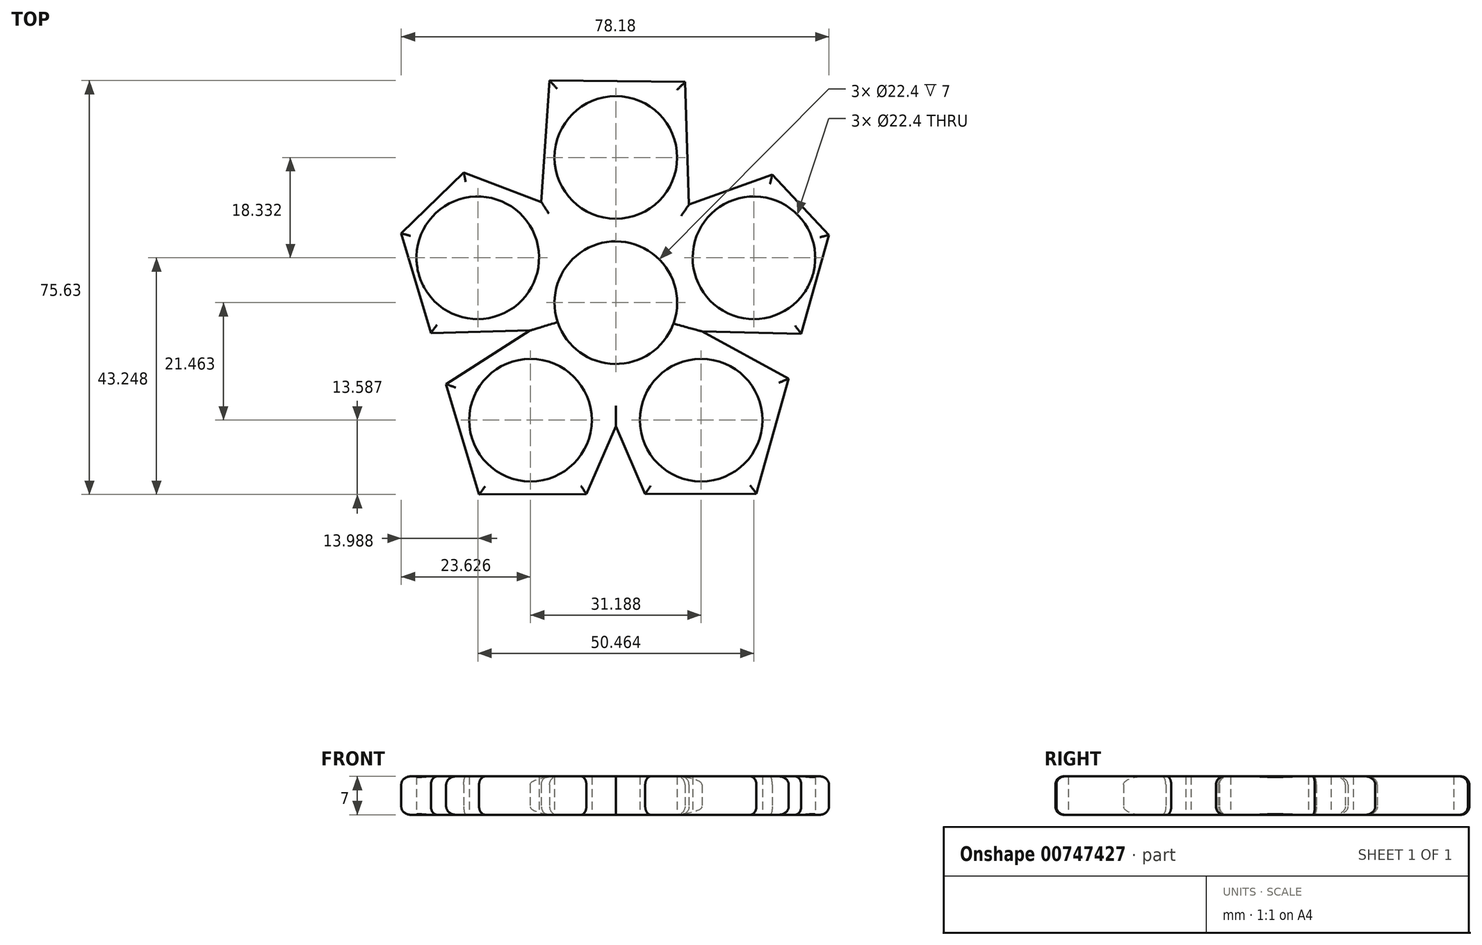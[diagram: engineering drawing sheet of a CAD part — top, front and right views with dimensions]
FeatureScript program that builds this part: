
annotation { "Feature Type Name" : "Feature", "Feature Type Description" : "" }
export const myFeature = defineFeature(function(context is Context, id is Id, definition is map)
    precondition{}
    {
        {
            var Q0;
            Q0=qCreatedBy(makeId("Top.planeOp"),FACE);
            var sketch = newSketch(context, id + "F0", { "sketchPlane" : qUnion([Q0])});
            skLineSegment(sketch, "E0.0", {"start": v(38.96, 12.36) * mm, "end": v(33.87, -5.71) * mm});
            skLineSegment(sketch, "E0.1", {"start": v(25.68, -34.87) * mm, "end": v(5.37, -34.94) * mm});
            skLineSegment(sketch, "E0.2", {"start": v(-25, -35.05) * mm, "end": v(-31.01, -14.87) * mm});
            skLineSegment(sketch, "E0.3", {"start": v(-39.22, 12.66) * mm, "end": v(-27.8, 23.78) * mm});
            skLineSegment(sketch, "E0.4", {"start": v(-12.12, 40.58) * mm, "end": v(12.67, 40.33) * mm});
            skLineSegment(sketch, "E0.5", {"start": v(28.58, 23.4) * mm, "end": v(38.96, 12.36) * mm});
            skPoint(sketch, "E0.0.midPoint", {"position": v(32.32, -11.25) * mm});
            skCircle(sketch, "E1", {"center": v(0, 0) * mm, "radius": 11.2 * mm});
            skCircle(sketch, "E2", {"center": v(0, 26.53) * mm, "radius": 11.2 * mm});
            skCircle(sketch, "E3.1.1", {"center": v(-25.23, 8.2) * mm, "radius": 11.2 * mm});
            skCircle(sketch, "E3.2.1", {"center": v(-15.6, -21.46) * mm, "radius": 11.2 * mm});
            skCircle(sketch, "E3.3.1", {"center": v(15.6, -21.46) * mm, "radius": 11.2 * mm});
            skCircle(sketch, "E3.4.1", {"center": v(25.23, 8.2) * mm, "radius": 11.2 * mm});
            skLineSegment(sketch, "E4.1", {"start": v(-5.39, -34.98) * mm, "end": v(0, -22.6) * mm});
            skLineSegment(sketch, "E4.2", {"start": v(0, -22.6) * mm, "end": v(5.37, -34.94) * mm});
            skPoint(sketch, "E4.0.midPoint", {"position": v(0, -51.18) * mm});
            skLineSegment(sketch, "E5.trimOffspring", {"start": v(-5.39, -34.98) * mm, "end": v(-25, -35.05) * mm});
            skLineSegment(sketch, "E6.1.0", {"start": v(15.74, -5.24) * mm, "end": v(33.87, -5.71) * mm});
            skLineSegment(sketch, "E6.1.2", {"start": v(31.58, -13.88) * mm, "end": v(15.74, -5.24) * mm});
            skLineSegment(sketch, "E6.2.0", {"start": v(13.37, 17.94) * mm, "end": v(12.63, 40.33) * mm});
            skLineSegment(sketch, "E6.2.2", {"start": v(28.58, 23.4) * mm, "end": v(13.37, 17.94) * mm});
            skLineSegment(sketch, "E6.3.0", {"start": v(-13.61, 18.4) * mm, "end": v(-27.8, 23.78) * mm});
            skLineSegment(sketch, "E6.3.2", {"start": v(-12.12, 40.58) * mm, "end": v(-13.61, 18.4) * mm});
            skLineSegment(sketch, "E6.4.0", {"start": v(-15.65, -5.08) * mm, "end": v(-31.01, -14.87) * mm});
            skLineSegment(sketch, "E6.4.2", {"start": v(-33.79, -5.56) * mm, "end": v(-15.65, -5.08) * mm});
            skLineSegment(sketch, "E7.trimOffspring", {"start": v(-33.79, -5.56) * mm, "end": v(-39.22, 12.66) * mm});
            skLineSegment(sketch, "E8.trimOffspring", {"start": v(31.58, -13.88) * mm, "end": v(25.68, -34.87) * mm});
            skPoint(sketch, "E9.orphan", {"position": v(-12.43, -51.18) * mm});
            skPoint(sketch, "E10.orphan", {"position": v(12.43, -51.18) * mm});
            skPoint(sketch, "E11.orphan", {"position": v(-46.73, -24.88) * mm});
            skPoint(sketch, "E12.orphan", {"position": v(-11.6, 48.23) * mm});
            skPoint(sketch, "E13.orphan", {"position": v(41.3, 27.95) * mm});
            skPoint(sketch, "E4.cCircle.center.orphan", {"position": v(0, -44) * mm});
            skSolve(sketch);
        }
        {
            var Q0;
            Q0=makeQuery(id+"F0.imprint","IMPRINT",FACE,{"disambiguationData":[TD([[makeQuery(id+"F0.imprint","IMPRINT",EDGE,{"derivedFrom":sQuery(id+"F0.wireOp",EDGE,"E0.0")}),-1.0]])]});
            extrude(context, id + "F1", {"entities" : qUnion([Q0]), "depth" : 7 * mm, "offsetDistance" : 25 * mm});
        }
        {
            var Q0;
            Q0=makeQuery(id+"F1.opExtrude","CAP_EDGE",EDGE,{"disambiguationData":[OSD([sQuery(id+"F0.wireOp",EDGE,"E0.2")])],"isStart":false});
            var Q1;
            Q1=makeQuery(id+"F1.opExtrude","CAP_EDGE",EDGE,{"disambiguationData":[OSD([sQuery(id+"F0.wireOp",EDGE,"E6.4.2")])],"isStart":false});
            var Q2;
            Q2=makeQuery(id+"F1.opExtrude","CAP_EDGE",EDGE,{"disambiguationData":[OSD([sQuery(id+"F0.wireOp",EDGE,"E6.4.0")])],"isStart":false});
            var Q3;
            Q3=makeQuery(id+"F1.opExtrude","CAP_EDGE",EDGE,{"disambiguationData":[OSD([sQuery(id+"F0.wireOp",EDGE,"E7.trimOffspring")])],"isStart":false});
            var Q4;
            Q4=makeQuery(id+"F1.opExtrude","CAP_EDGE",EDGE,{"disambiguationData":[OSD([sQuery(id+"F0.wireOp",EDGE,"E0.3")])],"isStart":false});
            var Q5;
            Q5=makeQuery(id+"F1.opExtrude","CAP_EDGE",EDGE,{"disambiguationData":[OSD([sQuery(id+"F0.wireOp",EDGE,"E6.3.0")])],"isStart":false});
            var Q6;
            Q6=makeQuery(id+"F1.opExtrude","CAP_EDGE",EDGE,{"disambiguationData":[OSD([sQuery(id+"F0.wireOp",EDGE,"E5.trimOffspring")])],"isStart":false});
            var Q7;
            Q7=makeQuery(id+"F1.opExtrude","CAP_EDGE",EDGE,{"disambiguationData":[OSD([sQuery(id+"F0.wireOp",EDGE,"E4.1")])],"isStart":false});
            var Q8;
            Q8=makeQuery(id+"F1.opExtrude","CAP_EDGE",EDGE,{"disambiguationData":[OSD([sQuery(id+"F0.wireOp",EDGE,"E4.2")])],"isStart":false});
            var Q9;
            Q9=makeQuery(id+"F1.opExtrude","CAP_EDGE",EDGE,{"disambiguationData":[OSD([sQuery(id+"F0.wireOp",EDGE,"E0.1")])],"isStart":false});
            var Q10;
            Q10=makeQuery(id+"F1.opExtrude","CAP_EDGE",EDGE,{"disambiguationData":[OSD([sQuery(id+"F0.wireOp",EDGE,"E8.trimOffspring")])],"isStart":false});
            var Q11;
            Q11=makeQuery(id+"F1.opExtrude","CAP_EDGE",EDGE,{"disambiguationData":[OSD([sQuery(id+"F0.wireOp",EDGE,"E6.1.2")])],"isStart":false});
            var Q12;
            Q12=makeQuery(id+"F1.opExtrude","CAP_EDGE",EDGE,{"disambiguationData":[OSD([sQuery(id+"F0.wireOp",EDGE,"E6.1.0")])],"isStart":false});
            var Q13;
            Q13=makeQuery(id+"F1.opExtrude","CAP_EDGE",EDGE,{"disambiguationData":[OSD([sQuery(id+"F0.wireOp",EDGE,"E0.0")])],"isStart":false});
            var Q14;
            Q14=makeQuery(id+"F1.opExtrude","CAP_EDGE",EDGE,{"disambiguationData":[OSD([sQuery(id+"F0.wireOp",EDGE,"E0.5")])],"isStart":false});
            var Q15;
            Q15=makeQuery(id+"F1.opExtrude","CAP_EDGE",EDGE,{"disambiguationData":[OSD([sQuery(id+"F0.wireOp",EDGE,"E6.2.0")])],"isStart":false});
            var Q16;
            Q16=makeQuery(id+"F1.opExtrude","CAP_EDGE",EDGE,{"disambiguationData":[OSD([sQuery(id+"F0.wireOp",EDGE,"E6.3.2")])],"isStart":false});
            var Q17;
            Q17=makeQuery(id+"F1.opExtrude","CAP_EDGE",EDGE,{"disambiguationData":[OSD([sQuery(id+"F0.wireOp",EDGE,"E6.2.2")])],"isStart":false});
            var Q18;
            Q18=makeQuery(id+"F1.opExtrude","CAP_EDGE",EDGE,{"disambiguationData":[OSD([sQuery(id+"F0.wireOp",EDGE,"E0.4")])],"isStart":false});
            fillet(context, id + "F2", {"entities" : qUnion([Q0, Q1, Q2, Q3, Q4, Q5, Q6, Q7, Q8, Q9, Q10, Q11, Q12, Q13, Q14, Q15, Q16, Q17, Q18]), "radius" : 1.5 * mm, "tangentPropagation" : true, "allowEdgeOverflow" : false});
        }
        {
            var Q0;
            Q0=makeQuery(id+"F1.opExtrude","CAP_EDGE",EDGE,{"disambiguationData":[OSD([sQuery(id+"F0.wireOp",EDGE,"E0.5")])],"isStart":true});
            var Q1;
            Q1=makeQuery(id+"F1.opExtrude","CAP_EDGE",EDGE,{"disambiguationData":[OSD([sQuery(id+"F0.wireOp",EDGE,"E6.1.0")])],"isStart":true});
            var Q2;
            Q2=makeQuery(id+"F1.opExtrude","CAP_EDGE",EDGE,{"disambiguationData":[OSD([sQuery(id+"F0.wireOp",EDGE,"E6.2.2")])],"isStart":true});
            var Q3;
            Q3=makeQuery(id+"F1.opExtrude","CAP_EDGE",EDGE,{"disambiguationData":[OSD([sQuery(id+"F0.wireOp",EDGE,"E6.2.0")])],"isStart":true});
            var Q4;
            Q4=makeQuery(id+"F1.opExtrude","CAP_EDGE",EDGE,{"disambiguationData":[OSD([sQuery(id+"F0.wireOp",EDGE,"E0.4")])],"isStart":true});
            var Q5;
            Q5=makeQuery(id+"F1.opExtrude","CAP_EDGE",EDGE,{"disambiguationData":[OSD([sQuery(id+"F0.wireOp",EDGE,"E6.4.0")])],"isStart":true});
            var Q6;
            Q6=makeQuery(id+"F1.opExtrude","CAP_EDGE",EDGE,{"disambiguationData":[OSD([sQuery(id+"F0.wireOp",EDGE,"E6.1.2")])],"isStart":true});
            var Q7;
            Q7=makeQuery(id+"F1.opExtrude","CAP_EDGE",EDGE,{"disambiguationData":[OSD([sQuery(id+"F0.wireOp",EDGE,"E6.3.0")])],"isStart":true});
            var Q8;
            Q8=makeQuery(id+"F1.opExtrude","CAP_EDGE",EDGE,{"disambiguationData":[OSD([sQuery(id+"F0.wireOp",EDGE,"E0.3")])],"isStart":true});
            var Q9;
            Q9=makeQuery(id+"F1.opExtrude","CAP_EDGE",EDGE,{"disambiguationData":[OSD([sQuery(id+"F0.wireOp",EDGE,"E8.trimOffspring")])],"isStart":true});
            var Q10;
            Q10=makeQuery(id+"F1.opExtrude","CAP_EDGE",EDGE,{"disambiguationData":[OSD([sQuery(id+"F0.wireOp",EDGE,"E4.1")])],"isStart":true});
            var Q11;
            Q11=makeQuery(id+"F1.opExtrude","CAP_EDGE",EDGE,{"disambiguationData":[OSD([sQuery(id+"F0.wireOp",EDGE,"E0.1")])],"isStart":true});
            var Q12;
            Q12=makeQuery(id+"F1.opExtrude","CAP_EDGE",EDGE,{"disambiguationData":[OSD([sQuery(id+"F0.wireOp",EDGE,"E5.trimOffspring")])],"isStart":true});
            var Q13;
            Q13=makeQuery(id+"F1.opExtrude","CAP_EDGE",EDGE,{"disambiguationData":[OSD([sQuery(id+"F0.wireOp",EDGE,"E6.3.2")])],"isStart":true});
            var Q14;
            Q14=makeQuery(id+"F1.opExtrude","CAP_EDGE",EDGE,{"disambiguationData":[OSD([sQuery(id+"F0.wireOp",EDGE,"E0.2")])],"isStart":true});
            var Q15;
            Q15=makeQuery(id+"F1.opExtrude","CAP_EDGE",EDGE,{"disambiguationData":[OSD([sQuery(id+"F0.wireOp",EDGE,"E6.4.2")])],"isStart":true});
            var Q16;
            Q16=makeQuery(id+"F1.opExtrude","CAP_EDGE",EDGE,{"disambiguationData":[OSD([sQuery(id+"F0.wireOp",EDGE,"E4.2")])],"isStart":true});
            var Q17;
            Q17=makeQuery(id+"F1.opExtrude","CAP_EDGE",EDGE,{"disambiguationData":[OSD([sQuery(id+"F0.wireOp",EDGE,"E0.0")])],"isStart":true});
            var Q18;
            Q18=makeQuery(id+"F1.opExtrude","CAP_EDGE",EDGE,{"disambiguationData":[OSD([sQuery(id+"F0.wireOp",EDGE,"E7.trimOffspring")])],"isStart":true});
            fillet(context, id + "F3", {"entities" : qUnion([Q0, Q1, Q2, Q3, Q4, Q5, Q6, Q7, Q8, Q9, Q10, Q11, Q12, Q13, Q14, Q15, Q16, Q17, Q18]), "radius" : 1.5 * mm, "tangentPropagation" : true, "allowEdgeOverflow" : false});
        }
    });
